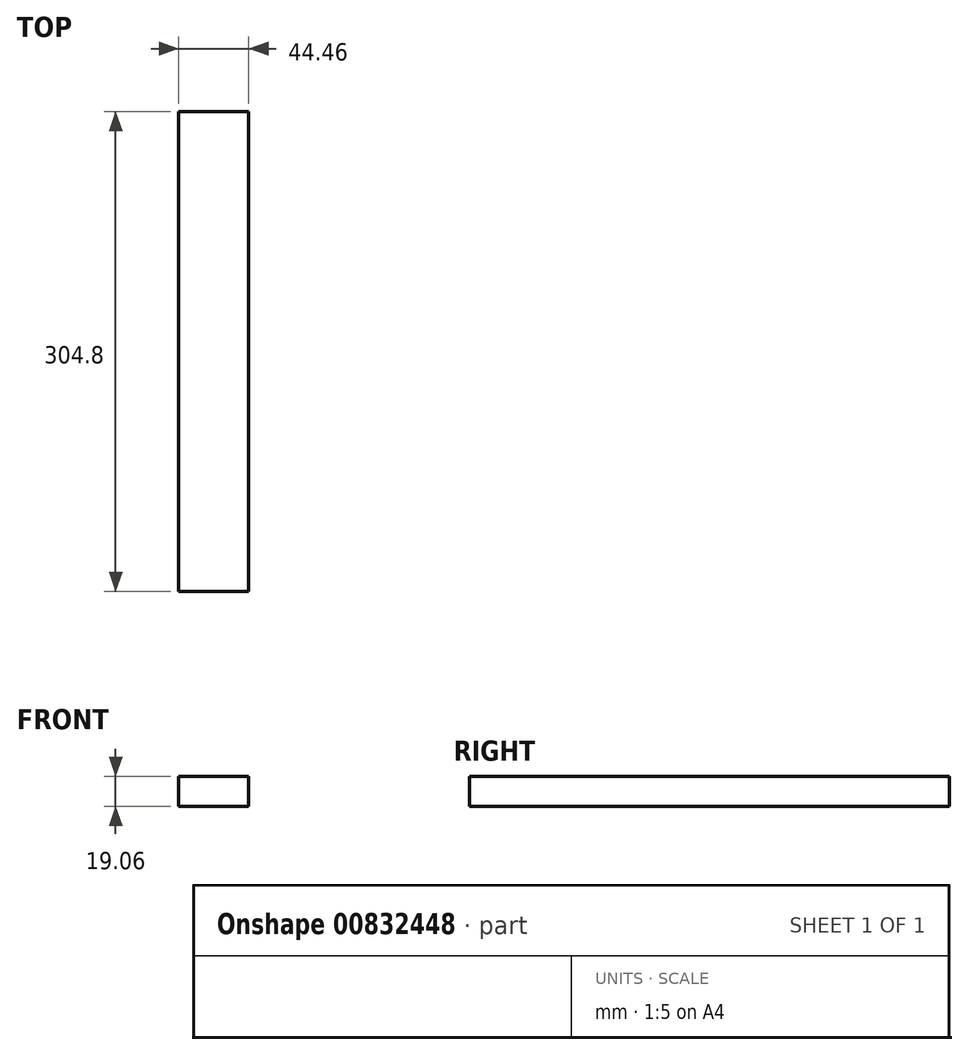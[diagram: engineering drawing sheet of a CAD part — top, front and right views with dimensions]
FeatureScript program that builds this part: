
annotation { "Feature Type Name" : "Feature", "Feature Type Description" : "" }
export const myFeature = defineFeature(function(context is Context, id is Id, definition is map)
    precondition{}
    {
        {
            var Q0;
            Q0=qCreatedBy(makeId("Front.planeOp"),FACE);
            var sketch = newSketch(context, id + "F0", { "sketchPlane" : qUnion([Q0])});
            skLineSegment(sketch, "E0.bottom", {"start": v(22.23, -9.52) * mm, "end": v(-22.23, -9.53) * mm});
            skLineSegment(sketch, "E0.top", {"start": v(22.23, 9.53) * mm, "end": v(-22.23, 9.52) * mm});
            skLineSegment(sketch, "E0.left", {"start": v(22.23, -9.52) * mm, "end": v(22.22, 9.53) * mm});
            skLineSegment(sketch, "E0.right", {"start": v(-22.23, -9.53) * mm, "end": v(-22.23, 9.52) * mm});
            skPoint(sketch, "E0.middle", {"position": v(0, 0) * mm});
            skLineSegment(sketch, "E1", {"start": v(9.1, -9.52) * mm, "end": v(9.1, -58.2) * mm, "construction": true});
            skSolve(sketch);
        }
        {
            var Q0;
            Q0=makeQuery(id+"F0.imprint","IMPRINT",FACE,{"disambiguationData":[TD([[makeQuery(id+"F0.imprint","IMPRINT",EDGE,{"derivedFrom":sQuery(id+"F0.wireOp",EDGE,"E0.bottom")}),-1.0]])]});
            extrude(context, id + "F1", {"entities" : qUnion([Q0]), "depth" : 304.8 * mm, "offsetDistance" : 25.4 * mm});
        }
    });
